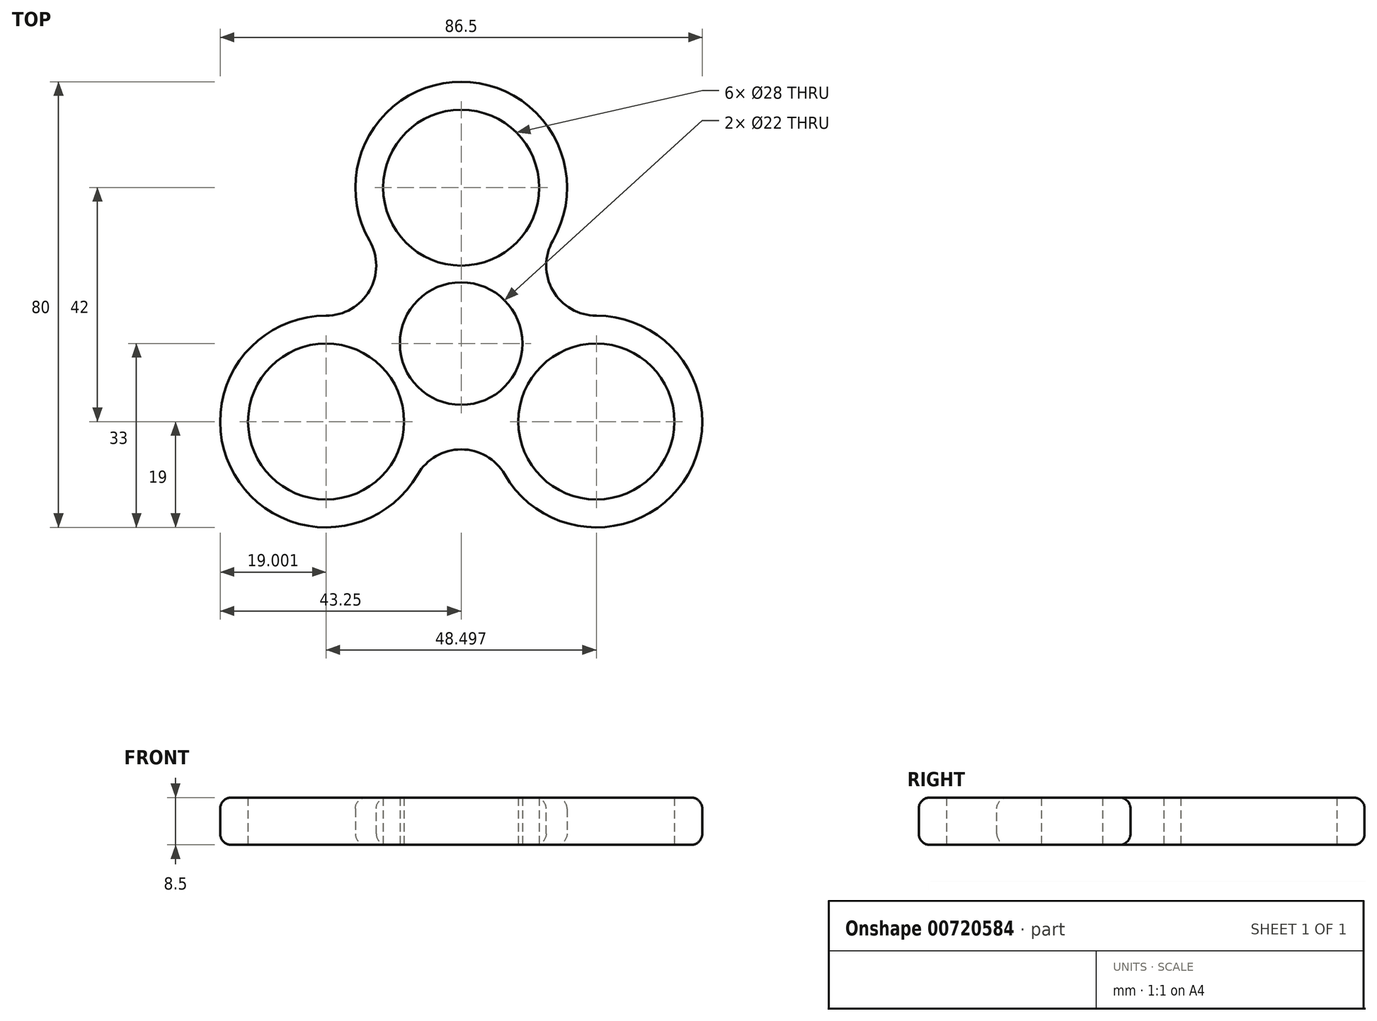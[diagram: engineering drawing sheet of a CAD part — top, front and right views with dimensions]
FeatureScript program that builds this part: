
annotation { "Feature Type Name" : "Feature", "Feature Type Description" : "" }
export const myFeature = defineFeature(function(context is Context, id is Id, definition is map)
    precondition{}
    {
        {
            var Q0;
            Q0=qCreatedBy(makeId("Top.planeOp"),FACE);
            var sketch = newSketch(context, id + "F0", { "sketchPlane" : qUnion([Q0])});
            skCircle(sketch, "E0", {"center": v(0, 0) * mm, "radius": 11 * mm});
            skLineSegment(sketch, "E1", {"start": v(0, 0) * mm, "end": v(0, 28) * mm});
            skCircle(sketch, "E2", {"center": v(0, 28) * mm, "radius": 14 * mm});
            skLineSegment(sketch, "E3", {"start": v(0, 0) * mm, "end": v(24.25, -14) * mm});
            skLineSegment(sketch, "E4", {"start": v(0, 0) * mm, "end": v(-24.25, -14) * mm});
            skCircle(sketch, "E5", {"center": v(24.25, -14) * mm, "radius": 14 * mm});
            skCircle(sketch, "E6", {"center": v(-24.25, -14) * mm, "radius": 14 * mm});
            skArc(sketch, "E7", {"start": v(-12.85, 14) * mm, "mid": v(-16.45, 9.5) * mm, "end": v(-18.55, 4.12) * mm});
            skArc(sketch, "E8.0", {"start": v(12.85, 14) * mm, "mid": v(0, 47) * mm, "end": v(-12.85, 14) * mm});
            skArc(sketch, "E9", {"start": v(5.7, -18.12) * mm, "mid": v(40.7, -23.5) * mm, "end": v(18.55, 4.12) * mm});
            skArc(sketch, "E10", {"start": v(-18.55, 4.12) * mm, "mid": v(-40.7, -23.5) * mm, "end": v(-5.7, -18.12) * mm});
            skArc(sketch, "E11.trimOffspring", {"start": v(18.55, 4.12) * mm, "mid": v(15, 11.65) * mm, "end": v(8.6, 16.95) * mm});
            skArc(sketch, "E12.trimOffspring", {"start": v(-5.7, -18.12) * mm, "mid": v(0, -19) * mm, "end": v(5.7, -18.12) * mm});
            skSolve(sketch);
        }
        {
            var Q0;
            Q0=makeQuery(id+"F0.imprint","IMPRINT",FACE,{"disambiguationData":[TD([[makeQuery(id+"F0.imprint","IMPRINT",EDGE,{"derivedFrom":sQuery(id+"F0.wireOp",EDGE,"E5")}),-1.0]])]});
            extrude(context, id + "F1", {"entities" : qUnion([Q0]), "depth" : 8.5 * mm, "offsetDistance" : 25 * mm});
        }
        {
            var Q0;
            Q0=makeQuery(id+"F1.opExtrude","SWEPT_EDGE",EDGE,{"disambiguationData":[OSD([sQuery(id+"F0.wireOp",EDGE,"E7"),sQuery(id+"F0.wireOp",EDGE,"E8.0")])]});
            var Q1;
            Q1=makeQuery(id+"F1.opExtrude","SWEPT_EDGE",EDGE,{"disambiguationData":[OSD([sQuery(id+"F0.wireOp",EDGE,"E7"),sQuery(id+"F0.wireOp",EDGE,"E10")])]});
            var Q2;
            Q2=makeQuery(id+"F1.opExtrude","SWEPT_EDGE",EDGE,{"disambiguationData":[OSD([sQuery(id+"F0.wireOp",EDGE,"E10"),sQuery(id+"F0.wireOp",EDGE,"E12.trimOffspring")])]});
            var Q3;
            Q3=makeQuery(id+"F1.opExtrude","SWEPT_EDGE",EDGE,{"disambiguationData":[OSD([sQuery(id+"F0.wireOp",EDGE,"E9"),sQuery(id+"F0.wireOp",EDGE,"E12.trimOffspring")])]});
            var Q4;
            Q4=makeQuery(id+"F1.opExtrude","SWEPT_EDGE",EDGE,{"disambiguationData":[OSD([sQuery(id+"F0.wireOp",EDGE,"E8.0"),sQuery(id+"F0.wireOp",EDGE,"E11.trimOffspring")])]});
            var Q5;
            Q5=makeQuery(id+"F1.opExtrude","SWEPT_EDGE",EDGE,{"disambiguationData":[OSD([sQuery(id+"F0.wireOp",EDGE,"E9"),sQuery(id+"F0.wireOp",EDGE,"E11.trimOffspring")])]});
            fillet(context, id + "F2", {"entities" : qUnion([Q0, Q1, Q2, Q3, Q4, Q5]), "radius" : 9 * mm, "tangentPropagation" : true, "allowEdgeOverflow" : false});
        }
        {
            var Q0;
            {var subQ0=sQuery(id+"F0.wireOp",EDGE,"E11.trimOffspring");var subQ1=sQuery(id+"F0.wireOp",EDGE,"E8.0");Q0=makeQuery(id+"F2.opFillet","BLEND_EDGE",EDGE,{"blendedFrom":[makeQuery(id+"F1.opExtrude","SWEPT_EDGE",EDGE,{"disambiguationData":[OSD([subQ1,subQ0])]}),makeQuery(id+"F1.opExtrude","CAP_FACE",FACE,{"disambiguationData":[OSD([sQuery(id+"F0.wireOp",EDGE,"E0"),sQuery(id+"F0.wireOp",EDGE,"E2"),sQuery(id+"F0.wireOp",EDGE,"E5"),sQuery(id+"F0.wireOp",EDGE,"E6"),sQuery(id+"F0.wireOp",EDGE,"E7"),subQ1,sQuery(id+"F0.wireOp",EDGE,"E9"),sQuery(id+"F0.wireOp",EDGE,"E10"),subQ0,sQuery(id+"F0.wireOp",EDGE,"E12.trimOffspring")])],"isStart":false})],"blendedInto":[makeQuery(id+"F1.opExtrude","CAP_FACE",FACE,{"disambiguationData":[OSD([sQuery(id+"F0.wireOp",EDGE,"E0"),sQuery(id+"F0.wireOp",EDGE,"E2"),sQuery(id+"F0.wireOp",EDGE,"E5"),sQuery(id+"F0.wireOp",EDGE,"E6"),sQuery(id+"F0.wireOp",EDGE,"E7"),subQ1,sQuery(id+"F0.wireOp",EDGE,"E9"),sQuery(id+"F0.wireOp",EDGE,"E10"),subQ0,sQuery(id+"F0.wireOp",EDGE,"E12.trimOffspring")])],"isStart":false})]});}
            var Q1;
            Q1=makeQuery(id+"F1.opExtrude","CAP_EDGE",EDGE,{"disambiguationData":[OSD([sQuery(id+"F0.wireOp",EDGE,"E8.0")])],"isStart":true});
            fillet(context, id + "F3", {"entities" : qUnion([Q0, Q1]), "radius" : 2 * mm, "tangentPropagation" : true, "allowEdgeOverflow" : false});
        }
    });
